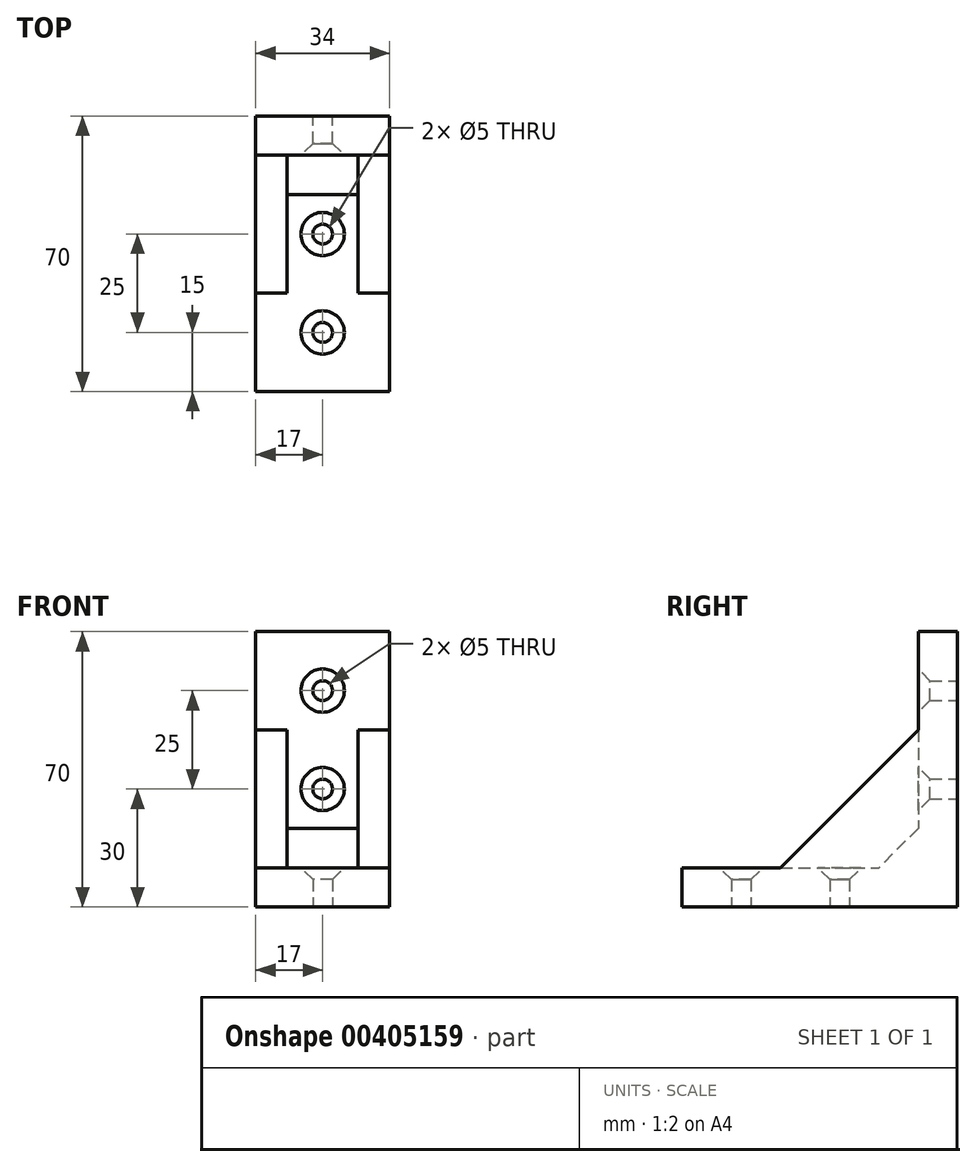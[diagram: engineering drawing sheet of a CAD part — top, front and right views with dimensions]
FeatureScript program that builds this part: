
annotation { "Feature Type Name" : "Feature", "Feature Type Description" : "" }
export const myFeature = defineFeature(function(context is Context, id is Id, definition is map)
    precondition{}
    {
        {
            var Q0;
            Q0=qCreatedBy(makeId("Right.planeOp"),FACE);
            var sketch = newSketch(context, id + "F0", { "sketchPlane" : qUnion([Q0])});
            skLineSegment(sketch, "E0", {"start": v(0, 0) * mm, "end": v(-70, 0) * mm});
            skLineSegment(sketch, "E1", {"start": v(-70, 0) * mm, "end": v(-70, 10) * mm});
            skLineSegment(sketch, "E2", {"start": v(-70, 10) * mm, "end": v(-20, 10) * mm});
            skLineSegment(sketch, "E3", {"start": v(-10, 20) * mm, "end": v(-10, 70) * mm});
            skLineSegment(sketch, "E4", {"start": v(-10, 70) * mm, "end": v(0, 70) * mm});
            skLineSegment(sketch, "E5", {"start": v(0, 70) * mm, "end": v(0, 0) * mm});
            skLineSegment(sketch, "E6", {"start": v(-10, 70) * mm, "end": v(-10, 20) * mm});
            skLineSegment(sketch, "E7", {"start": v(-20, 10) * mm, "end": v(-10, 20) * mm});
            skSolve(sketch);
        }
        {
            var Q0;
            Q0 = qSketchRegion(id + "F0", true);
            extrude(context, id + "F1", {"entities" : qUnion([Q0]), "endBound" : BoundingType.SYMMETRIC, "depth" : 34 * mm});
        }
        {
            var Q0;
            Q0=qCreatedBy(makeId("Front.planeOp"),FACE);
            var sketch = newSketch(context, id + "F2", { "sketchPlane" : qUnion([Q0])});
            skLineSegment(sketch, "E8", {"start": v(0, 0) * mm, "end": v(0, 30) * mm});
            skLineSegment(sketch, "E9", {"start": v(0, 30) * mm, "end": v(0, 55) * mm});
            skCircle(sketch, "E10", {"center": v(0, 55) * mm, "radius": 2.5 * mm});
            skCircle(sketch, "E11", {"center": v(0, 30) * mm, "radius": 2.5 * mm});
            skSolve(sketch);
        }
        {
            var Q0;
            Q0 = qSketchRegion(id + "F2", true);
            extrude(context, id + "F3", {"entities" : qUnion([Q0]), "depth" : 25 * mm});
        }
        {
            var Q0;
            Q0=makeQuery(id+"F3.opExtrude","SWEPT_BODY",BODY,{"disambiguationData":[OSD([sQuery(id+"F2.wireOp",EDGE,"E10")])]});
            var Q1;
            Q1=makeQuery(id+"F3.opExtrude","SWEPT_BODY",BODY,{"disambiguationData":[OSD([sQuery(id+"F2.wireOp",EDGE,"E11")])]});
            var Q2;
            Q2=makeQuery(id+"F1.opExtrude","SWEPT_BODY",BODY,{"disambiguationData":[OSD([sQuery(id+"F0.wireOp",EDGE,"E0"),sQuery(id+"F0.wireOp",EDGE,"E1"),sQuery(id+"F0.wireOp",EDGE,"E2"),sQuery(id+"F0.wireOp",EDGE,"E3"),sQuery(id+"F0.wireOp",EDGE,"E4"),sQuery(id+"F0.wireOp",EDGE,"E5")])]});
            booleanBodies(context, id + "F4", {"operationType" : BooleanOperationType.SUBTRACTION, "tools" : qUnion([Q0, Q1]), "targets" : qUnion([Q2])});
        }
        {
            var Q0;
            Q0=qCreatedBy(makeId("Top.planeOp"),FACE);
            var sketch = newSketch(context, id + "F5", { "sketchPlane" : qUnion([Q0])});
            skLineSegment(sketch, "E12", {"start": v(0, 0) * mm, "end": v(0, -30) * mm});
            skLineSegment(sketch, "E13", {"start": v(0, -30) * mm, "end": v(0, -55) * mm});
            skCircle(sketch, "E14", {"center": v(0, -30) * mm, "radius": 2.5 * mm});
            skCircle(sketch, "E15", {"center": v(0, -55) * mm, "radius": 2.5 * mm});
            skSolve(sketch);
        }
        {
            var Q0;
            Q0 = qSketchRegion(id + "F5", true);
            extrude(context, id + "F6", {"entities" : qUnion([Q0]), "depth" : 25 * mm});
        }
        {
            var Q0;
            Q0=makeQuery(id+"F6.opExtrude","SWEPT_BODY",BODY,{"disambiguationData":[OSD([sQuery(id+"F5.wireOp",EDGE,"E14")])]});
            var Q1;
            Q1=makeQuery(id+"F6.opExtrude","SWEPT_BODY",BODY,{"disambiguationData":[OSD([sQuery(id+"F5.wireOp",EDGE,"E15")])]});
            var Q2;
            Q2=makeQuery(id+"F1.opExtrude","SWEPT_BODY",BODY,{"disambiguationData":[OSD([sQuery(id+"F0.wireOp",EDGE,"E0"),sQuery(id+"F0.wireOp",EDGE,"E1"),sQuery(id+"F0.wireOp",EDGE,"E2"),sQuery(id+"F0.wireOp",EDGE,"E3"),sQuery(id+"F0.wireOp",EDGE,"E4"),sQuery(id+"F0.wireOp",EDGE,"E5")])]});
            booleanBodies(context, id + "F7", {"operationType" : BooleanOperationType.SUBTRACTION, "tools" : qUnion([Q0, Q1]), "targets" : qUnion([Q2])});
        }
        {
            var Q0;
            Q0=makeQuery(id+"F7.opBoolean","INTERSECT",EDGE,{"derivedFrom":[makeQuery(id+"F1.opExtrude","SWEPT_FACE",FACE,{"disambiguationData":[OSD([sQuery(id+"F0.wireOp",EDGE,"E2")])]}),makeQuery(id+"F6.opExtrude","SWEPT_FACE",FACE,{"disambiguationData":[OSD([sQuery(id+"F5.wireOp",EDGE,"E14")])]})]});
            var Q1;
            Q1=makeQuery(id+"F7.opBoolean","INTERSECT",EDGE,{"derivedFrom":[makeQuery(id+"F1.opExtrude","SWEPT_FACE",FACE,{"disambiguationData":[OSD([sQuery(id+"F0.wireOp",EDGE,"E2")])]}),makeQuery(id+"F6.opExtrude","SWEPT_FACE",FACE,{"disambiguationData":[OSD([sQuery(id+"F5.wireOp",EDGE,"E15")])]})]});
            var Q2;
            Q2=makeQuery(id+"F4.opBoolean","INTERSECT",EDGE,{"derivedFrom":[makeQuery(id+"F1.opExtrude","SWEPT_FACE",FACE,{"disambiguationData":[OSD([sQuery(id+"F0.wireOp",EDGE,"E3")])]}),makeQuery(id+"F3.opExtrude","SWEPT_FACE",FACE,{"disambiguationData":[OSD([sQuery(id+"F2.wireOp",EDGE,"E11")])]})]});
            var Q3;
            Q3=makeQuery(id+"F4.opBoolean","INTERSECT",EDGE,{"derivedFrom":[makeQuery(id+"F1.opExtrude","SWEPT_FACE",FACE,{"disambiguationData":[OSD([sQuery(id+"F0.wireOp",EDGE,"E3")])]}),makeQuery(id+"F3.opExtrude","SWEPT_FACE",FACE,{"disambiguationData":[OSD([sQuery(id+"F2.wireOp",EDGE,"E10")])]})]});
            chamfer(context, id + "F8", {"entities" : qUnion([Q0, Q1, Q2, Q3]), "width" : 3 * mm, "tangentPropagation" : true});
        }
        {
            var Q0;
            Q0=qCreatedBy(makeId("Right.planeOp"),FACE);
            var sketch = newSketch(context, id + "F9", { "sketchPlane" : qUnion([Q0])});
            skLineSegment(sketch, "E16", {"start": v(0, 0) * mm, "end": v(-70, 0) * mm});
            skLineSegment(sketch, "E17", {"start": v(-70, 0) * mm, "end": v(-70, 10) * mm});
            skLineSegment(sketch, "E18", {"start": v(-70, 10) * mm, "end": v(-45, 10) * mm});
            skLineSegment(sketch, "E19", {"start": v(-45, 10) * mm, "end": v(-45, 0) * mm});
            skLineSegment(sketch, "E20", {"start": v(0, 0) * mm, "end": v(0, 70) * mm});
            skLineSegment(sketch, "E21", {"start": v(0, 70) * mm, "end": v(-10, 70) * mm});
            skLineSegment(sketch, "E22", {"start": v(-10, 70) * mm, "end": v(-10, 45) * mm});
            skLineSegment(sketch, "E23", {"start": v(-10, 45) * mm, "end": v(-45, 10) * mm});
            skPoint(sketch, "E24.end.orphan", {"position": v(0, 45) * mm});
            skSolve(sketch);
        }
        {
            var Q0;
            Q0 = qSketchRegion(id + "F9", true);
            extrude(context, id + "F10", {"entities" : qUnion([Q0]), "endBound" : BoundingType.SYMMETRIC, "depth" : 8 * mm});
        }
        {
            var Q0;
            Q0=makeQuery(id+"F10.opExtrude","SWEPT_BODY",BODY,{"disambiguationData":[OSD([sQuery(id+"F9.wireOp",EDGE,"E16"),sQuery(id+"F9.wireOp",EDGE,"E17"),sQuery(id+"F9.wireOp",EDGE,"E18"),sQuery(id+"F9.wireOp",EDGE,"E20"),sQuery(id+"F9.wireOp",EDGE,"E21"),sQuery(id+"F9.wireOp",EDGE,"E22"),sQuery(id+"F9.wireOp",EDGE,"E23")])]});
            transform(context, id + "F11", {"entities" : qUnion([Q0]), "transformType" : TransformType.TRANSLATION_3D, "dx" : 13 * mm, "dy" : 0 * mm, "dz" : 0 * mm, "makeCopy" : false});
        }
        {
            var Q0;
            Q0=makeQuery(id+"F10.opExtrude","SWEPT_BODY",BODY,{"disambiguationData":[OSD([sQuery(id+"F9.wireOp",EDGE,"E16"),sQuery(id+"F9.wireOp",EDGE,"E17"),sQuery(id+"F9.wireOp",EDGE,"E18"),sQuery(id+"F9.wireOp",EDGE,"E20"),sQuery(id+"F9.wireOp",EDGE,"E21"),sQuery(id+"F9.wireOp",EDGE,"E22"),sQuery(id+"F9.wireOp",EDGE,"E23")])]});
            var Q1;
            Q1=qCreatedBy(makeId("Right.planeOp"),FACE);
            mirror(context, id + "F12", {"operationType" : NewBodyOperationType.ADD, "entities" : qUnion([Q0]), "mirrorPlane" : qUnion([Q1])});
        }
    });
